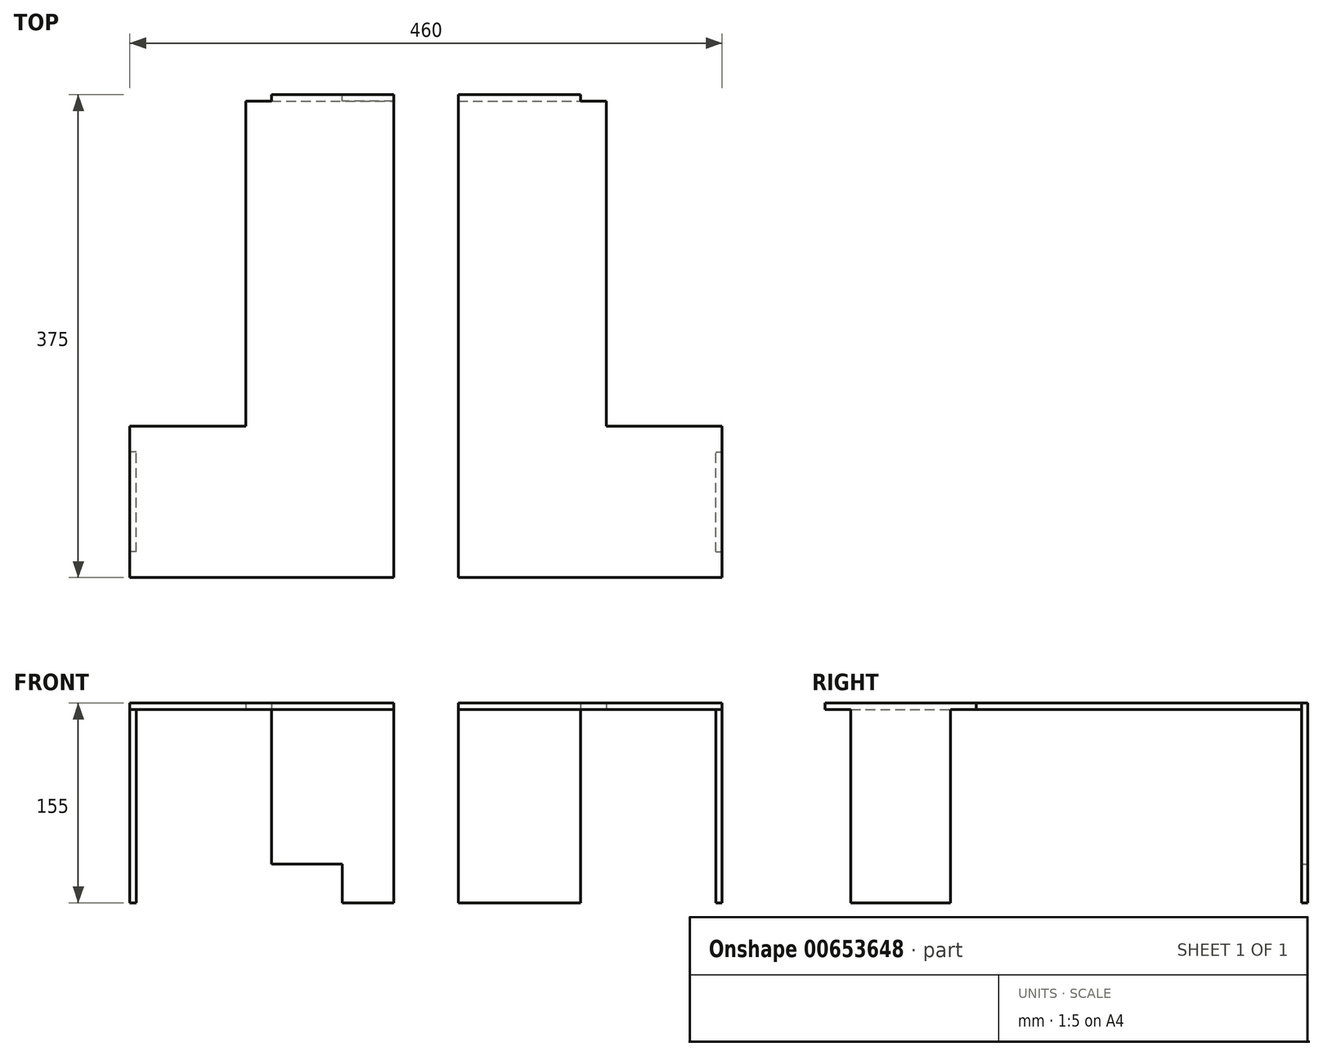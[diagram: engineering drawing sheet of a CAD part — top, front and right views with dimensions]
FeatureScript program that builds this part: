
annotation { "Feature Type Name" : "Feature", "Feature Type Description" : "" }
export const myFeature = defineFeature(function(context is Context, id is Id, definition is map)
    precondition{}
    {
        {
            var Q0;
            Q0=qCreatedBy(makeId("Top.planeOp"),FACE);
            var sketch = newSketch(context, id + "F0", { "sketchPlane" : qUnion([Q0])});
            skLineSegment(sketch, "E0.bottom", {"start": v(0, 0) * mm, "end": v(280, 0) * mm});
            skLineSegment(sketch, "E0.top", {"start": v(0, -370) * mm, "end": v(280, -370) * mm});
            skLineSegment(sketch, "E0.left", {"start": v(0, 0) * mm, "end": v(0, -370) * mm});
            skLineSegment(sketch, "E0.right", {"start": v(280, 0) * mm, "end": v(280, -370) * mm});
            skLineSegment(sketch, "E1.bottom", {"start": v(0, -370) * mm, "end": v(-90, -370) * mm});
            skLineSegment(sketch, "E1.top", {"start": v(0, -252.5) * mm, "end": v(-90, -252.5) * mm});
            skLineSegment(sketch, "E1.left", {"start": v(0, -370) * mm, "end": v(0, -252.5) * mm});
            skLineSegment(sketch, "E1.right", {"start": v(-90, -370) * mm, "end": v(-90, -252.5) * mm});
            skLineSegment(sketch, "E2.bottom", {"start": v(280, -370) * mm, "end": v(370, -370) * mm});
            skLineSegment(sketch, "E2.top", {"start": v(280, -252.5) * mm, "end": v(370, -252.5) * mm});
            skLineSegment(sketch, "E2.left", {"start": v(280, -370) * mm, "end": v(280, -252.5) * mm});
            skLineSegment(sketch, "E2.right", {"start": v(370, -370) * mm, "end": v(370, -252.5) * mm});
            skSolve(sketch);
        }
        {
            var Q0;
            Q0 = qSketchRegion(id + "F0", true);
            extrude(context, id + "F1", {"entities" : qUnion([Q0]), "depth" : 5 * mm, "offsetDistance" : 25 * mm});
        }
        {
            var Q0;
            Q0=makeQuery(id+"F1.opExtrude","CAP_FACE",FACE,{"disambiguationData":[OSD([sQuery(id+"F0.wireOp",EDGE,"E0.bottom"),sQuery(id+"F0.wireOp",EDGE,"E0.top"),sQuery(id+"F0.wireOp",EDGE,"E0.left"),sQuery(id+"F0.wireOp",EDGE,"E0.right"),sQuery(id+"F0.wireOp",EDGE,"E1.bottom"),sQuery(id+"F0.wireOp",EDGE,"E1.top"),sQuery(id+"F0.wireOp",EDGE,"E1.right"),sQuery(id+"F0.wireOp",EDGE,"E2.bottom"),sQuery(id+"F0.wireOp",EDGE,"E2.top"),sQuery(id+"F0.wireOp",EDGE,"E2.right")])],"isStart":false});
            var sketch = newSketch(context, id + "F2", { "sketchPlane" : qUnion([Q0])});
            skLineSegment(sketch, "E3.bottom", {"start": v(115, -370) * mm, "end": v(165, -370) * mm});
            skLineSegment(sketch, "E3.top", {"start": v(115, 0) * mm, "end": v(165, 0) * mm});
            skLineSegment(sketch, "E3.left", {"start": v(115, -370) * mm, "end": v(115, 0) * mm});
            skLineSegment(sketch, "E3.right", {"start": v(165, -370) * mm, "end": v(165, 0) * mm});
            skSolve(sketch);
        }
        {
            var Q0;
            Q0=makeQuery(id+"F2.imprint","IMPRINT",FACE,{"disambiguationData":[TD([[makeQuery(id+"F2.imprint","IMPRINT",EDGE,{"derivedFrom":sQuery(id+"F2.wireOp",EDGE,"E3.bottom")}),-1.0]])]});
            extrude(context, id + "F3", {"entities" : qUnion([Q0]), "operationType" : NewBodyOperationType.REMOVE, "oppositeDirection" : true, "depth" : 25 * mm, "offsetDistance" : 25 * mm});
        }
        {
            var Q0;
            {var subQ6=sQuery(id+"F0.wireOp",EDGE,"E0.right");var subQ9=sQuery(id+"F0.wireOp",EDGE,"E0.bottom");Q0=makeQuery(id+"F3.boolean.opBoolean","SPLIT",FACE,{"disambiguationData":[TD([makeQuery(id+"F1.opExtrude","SWEPT_FACE",FACE,{"disambiguationData":[OSD([subQ6])]})])],"derivedFrom":makeQuery(id+"F1.opExtrude","SWEPT_FACE",FACE,{"disambiguationData":[OSD([subQ9])]})});}
            var sketch = newSketch(context, id + "F4", { "sketchPlane" : qUnion([Q0])});
            skLineSegment(sketch, "E4.bottom", {"start": v(-260, 5) * mm, "end": v(-165, 5) * mm});
            skLineSegment(sketch, "E4.top", {"start": v(-260, -150) * mm, "end": v(-165, -150) * mm});
            skLineSegment(sketch, "E4.left", {"start": v(-260, 5) * mm, "end": v(-260, -150) * mm});
            skLineSegment(sketch, "E4.right", {"start": v(-165, 5) * mm, "end": v(-165, -150) * mm});
            skLineSegment(sketch, "E5.bottom", {"start": v(-115, 5) * mm, "end": v(-20, 5) * mm});
            skLineSegment(sketch, "E5.top", {"start": v(-115, -150) * mm, "end": v(-20, -150) * mm});
            skLineSegment(sketch, "E5.left", {"start": v(-115, 5) * mm, "end": v(-115, -150) * mm});
            skLineSegment(sketch, "E5.right", {"start": v(-20, 5) * mm, "end": v(-20, -150) * mm});
            skSolve(sketch);
        }
        {
            var Q0;
            Q0=makeQuery(id+"F1.opExtrude","SWEPT_FACE",FACE,{"disambiguationData":[OSD([sQuery(id+"F0.wireOp",EDGE,"E1.right")])]});
            var sketch = newSketch(context, id + "F5", { "sketchPlane" : qUnion([Q0])});
            skLineSegment(sketch, "E6.bottom", {"start": v(272.5, 0) * mm, "end": v(350, 0) * mm});
            skLineSegment(sketch, "E6.top", {"start": v(272.5, -150) * mm, "end": v(350, -150) * mm});
            skLineSegment(sketch, "E6.left", {"start": v(272.5, 0) * mm, "end": v(272.5, -150) * mm});
            skLineSegment(sketch, "E6.right", {"start": v(350, 0) * mm, "end": v(350, -150) * mm});
            skSolve(sketch);
        }
        {
            var Q0;
            Q0=makeQuery(id+"F1.opExtrude","SWEPT_FACE",FACE,{"disambiguationData":[OSD([sQuery(id+"F0.wireOp",EDGE,"E2.right")])]});
            var sketch = newSketch(context, id + "F6", { "sketchPlane" : qUnion([Q0])});
            skLineSegment(sketch, "E7.bottom", {"start": v(-350, -150) * mm, "end": v(-272.5, -150) * mm});
            skLineSegment(sketch, "E7.top", {"start": v(-350, 0) * mm, "end": v(-272.5, 0) * mm});
            skLineSegment(sketch, "E7.left", {"start": v(-350, -150) * mm, "end": v(-350, 0) * mm});
            skLineSegment(sketch, "E7.right", {"start": v(-272.5, -150) * mm, "end": v(-272.5, 0) * mm});
            skSolve(sketch);
        }
        {
            var Q0;
            Q0=makeQuery(id+"F5.imprint","IMPRINT",FACE,{"disambiguationData":[TD([[makeQuery(id+"F5.imprint","IMPRINT",EDGE,{"derivedFrom":sQuery(id+"F5.wireOp",EDGE,"E6.bottom")}),1.0]])]});
            extrude(context, id + "F7", {"entities" : qUnion([Q0]), "operationType" : NewBodyOperationType.ADD, "oppositeDirection" : true, "depth" : 5 * mm, "offsetDistance" : 25 * mm});
        }
        {
            var Q0;
            {var subQ0=sQuery(id+"F4.wireOp",EDGE,"E4.top");Q0=makeQuery(id+"F4.imprint","IMPRINT",FACE,{"disambiguationData":[TD([[makeQuery(id+"F4.imprint","IMPRINT",EDGE,{"derivedFrom":subQ0}),1.0]])]});}
            var Q1;
            Q1=makeQuery(id+"F4.imprint","IMPRINT",FACE,{"disambiguationData":[TD([[makeQuery(id+"F4.imprint","IMPRINT",EDGE,{"derivedFrom":sQuery(id+"F4.wireOp",EDGE,"E5.bottom")}),-1.0]])]});
            var Q2;
            {var subQ0=sQuery(id+"F4.wireOp",EDGE,"E4.bottom");Q2=makeQuery(id+"F4.imprint","IMPRINT",FACE,{"disambiguationData":[TD([[makeQuery(id+"F4.imprint","IMPRINT",EDGE,{"derivedFrom":subQ0}),1.0]])]});}
            extrude(context, id + "F8", {"entities" : qUnion([Q0, Q1, Q2]), "operationType" : NewBodyOperationType.ADD, "depth" : 5 * mm, "offsetDistance" : 25 * mm});
        }
        {
            var Q0;
            Q0=makeQuery(id+"F6.imprint","IMPRINT",FACE,{"disambiguationData":[TD([[makeQuery(id+"F6.imprint","IMPRINT",EDGE,{"derivedFrom":sQuery(id+"F6.wireOp",EDGE,"E7.bottom")}),1.0]])]});
            extrude(context, id + "F9", {"entities" : qUnion([Q0]), "operationType" : NewBodyOperationType.ADD, "oppositeDirection" : true, "depth" : 5 * mm, "offsetDistance" : 25 * mm});
        }
        {
            var Q0;
            Q0=makeQuery(id+"F8.opExtrude","CAP_FACE",FACE,{"disambiguationData":[OSD([sQuery(id+"F4.wireOp",EDGE,"E5.bottom"),sQuery(id+"F4.wireOp",EDGE,"E5.top"),sQuery(id+"F4.wireOp",EDGE,"E5.left"),sQuery(id+"F4.wireOp",EDGE,"E5.right")])],"isStart":false});
            var sketch = newSketch(context, id + "F10", { "sketchPlane" : qUnion([Q0])});
            skLineSegment(sketch, "E8.bottom", {"start": v(-20, -150) * mm, "end": v(-75, -150) * mm});
            skLineSegment(sketch, "E8.top", {"start": v(-20, -120) * mm, "end": v(-75, -120) * mm});
            skLineSegment(sketch, "E8.left", {"start": v(-20, -150) * mm, "end": v(-20, -120) * mm});
            skLineSegment(sketch, "E8.right", {"start": v(-75, -150) * mm, "end": v(-75, -120) * mm});
            skSolve(sketch);
        }
        {
            var Q0;
            Q0=makeQuery(id+"F10.imprint","IMPRINT",FACE,{"disambiguationData":[TD([[makeQuery(id+"F10.imprint","IMPRINT",EDGE,{"derivedFrom":sQuery(id+"F10.wireOp",EDGE,"E8.bottom")}),1.0]])]});
            extrude(context, id + "F11", {"entities" : qUnion([Q0]), "operationType" : NewBodyOperationType.REMOVE, "oppositeDirection" : true, "depth" : 25 * mm, "offsetDistance" : 25 * mm});
        }
    });
